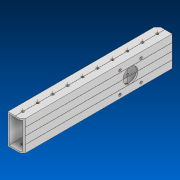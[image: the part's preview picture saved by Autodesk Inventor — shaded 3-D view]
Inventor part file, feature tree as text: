
AUTODESK INVENTOR PART (.ipt)
format: ipt  version: 2022 (Build 260153000, 153)  size: 548,864 bytes
history: native  units: in
note: dims shown in document units (in); Inventor stores cm internally (conversion verified against a paired STEP export)
features: other x16, extrude x3, sketch x3, pattern_linear x1, reference x1
ambient origin geometry x8: Origin, YZ Plane, XZ Plane, XY Plane, X Axis, Y Axis, Z Axis, Center Point
bodies: Solid1 (feature_tree)
feature tree (24):
  extrude  "Extrusion1"  Depth=2.0in
  other  "Work Axis1"
  pattern_linear  "Rectangular Pattern1"  Count1=10  [1 undecoded]
  extrude  "Extrusion2"  Depth=1.0in
  extrude  "Extrusion3"  TaperAngle=0.0deg  [1 undecoded]
  sketch  "Sketch1"  dims[d0=1.0in d1=2.0in]
  other  "Work Axis2"
  other  "Work Axis3"
  other  "Work Axis4"
  other  "Work Axis5"
  other  "Work Axis6"
  other  "Work Axis7"
  other  "Work Axis8"
  other  "Work Axis9"
  other  "Work Axis10"
  sketch  "Sketch2"  dims[d2=49.0in]
  sketch  "Sketch3"  dims[d3=0.0in d4=3.937in d6=1.0in d9=0.0in d10=0.0in d11=1.0in d12=0.0in d13=0.0in d14=0.17in d15=2.0in]
  reference  "Reference2"
  other  "Cut-Extrude2"
  parser-record x1  (decoder bookkeeping rows leaked as tree rows — omitted from the tree; the rows remain in map.json)
  other  "Chassis.iam"
  other  "VP Input to 2X Ring Gears to 90 Degree to VP Output:1"
  other  "Universal Female Output Shaft 1_2 Hex:1"
  other  "217-5839-006 Rev4_3"
note: 2 required parameter values undecoded (feature->parameter linkage not recoverable at this tier; creation-order binding heuristic only, values carry confidence <= 0.55)
note: 1 file-system path scrubbed to <path> (originals preserved in map.json)
